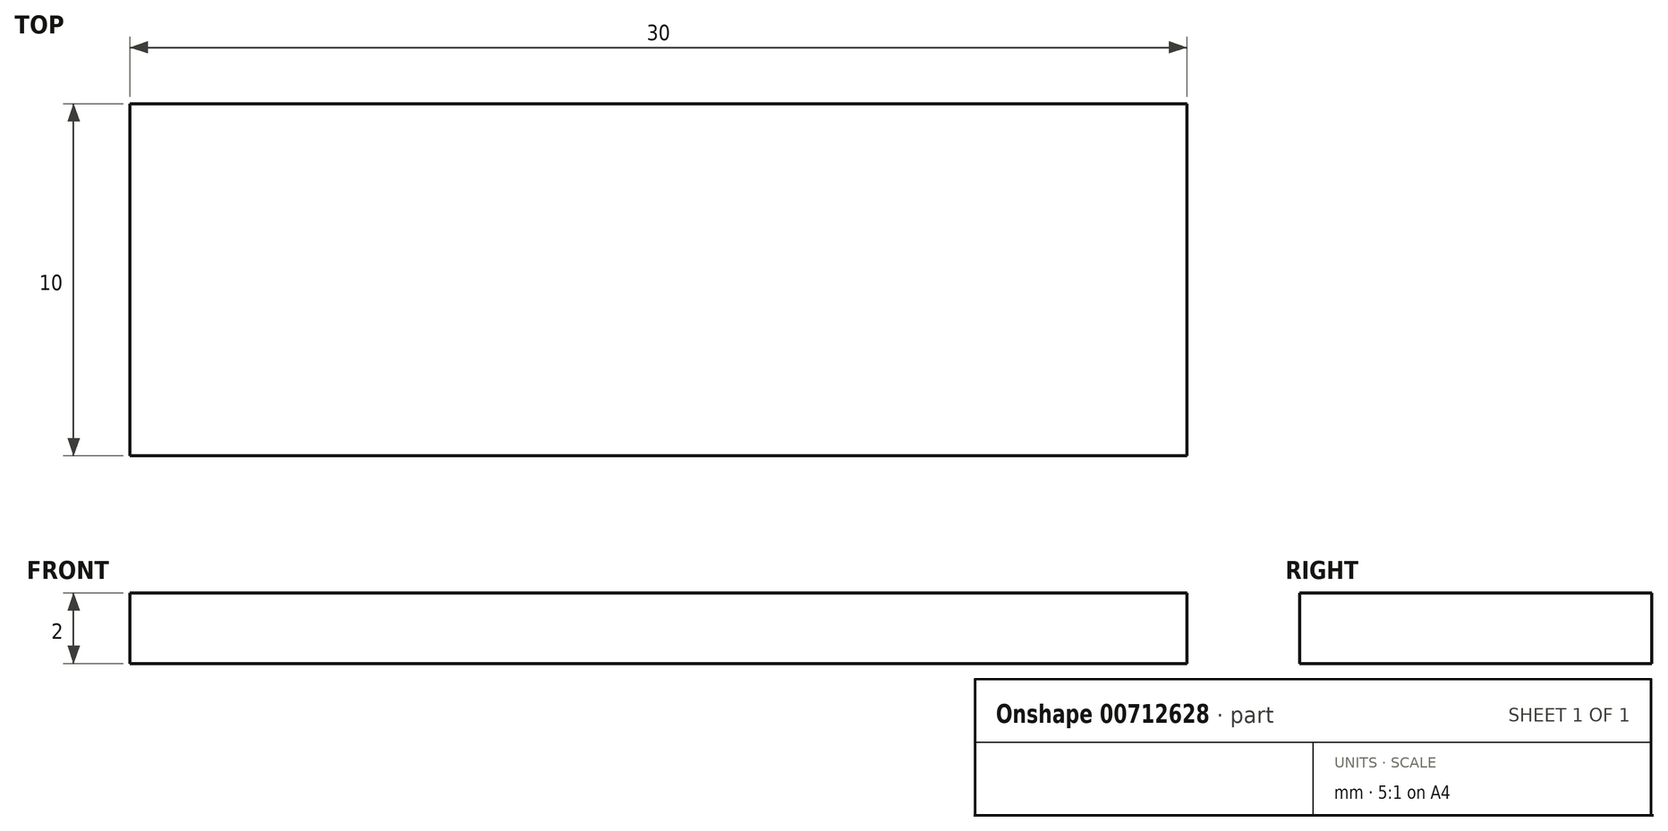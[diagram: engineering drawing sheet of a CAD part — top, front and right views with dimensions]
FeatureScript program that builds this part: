
annotation { "Feature Type Name" : "Feature", "Feature Type Description" : "" }
export const myFeature = defineFeature(function(context is Context, id is Id, definition is map)
    precondition{}
    {
        {
            var Q0;
            Q0=qCreatedBy(makeId("Top.planeOp"),FACE);
            var sketch = newSketch(context, id + "F0", { "sketchPlane" : qUnion([Q0])});
            skLineSegment(sketch, "E0.bottom", {"start": v(0, 0) * mm, "end": v(30, 0) * mm});
            skLineSegment(sketch, "E0.top", {"start": v(0, -10) * mm, "end": v(30, -10) * mm});
            skLineSegment(sketch, "E0.left", {"start": v(0, 0) * mm, "end": v(0, -10) * mm});
            skLineSegment(sketch, "E0.right", {"start": v(30, 0) * mm, "end": v(30, -10) * mm});
            skSolve(sketch);
        }
        {
            var Q0;
            Q0 = qSketchRegion(id + "F0", true);
            extrude(context, id + "F1", {"entities" : qUnion([Q0]), "depth" : 2 * mm, "offsetDistance" : 25 * mm});
        }
    });
